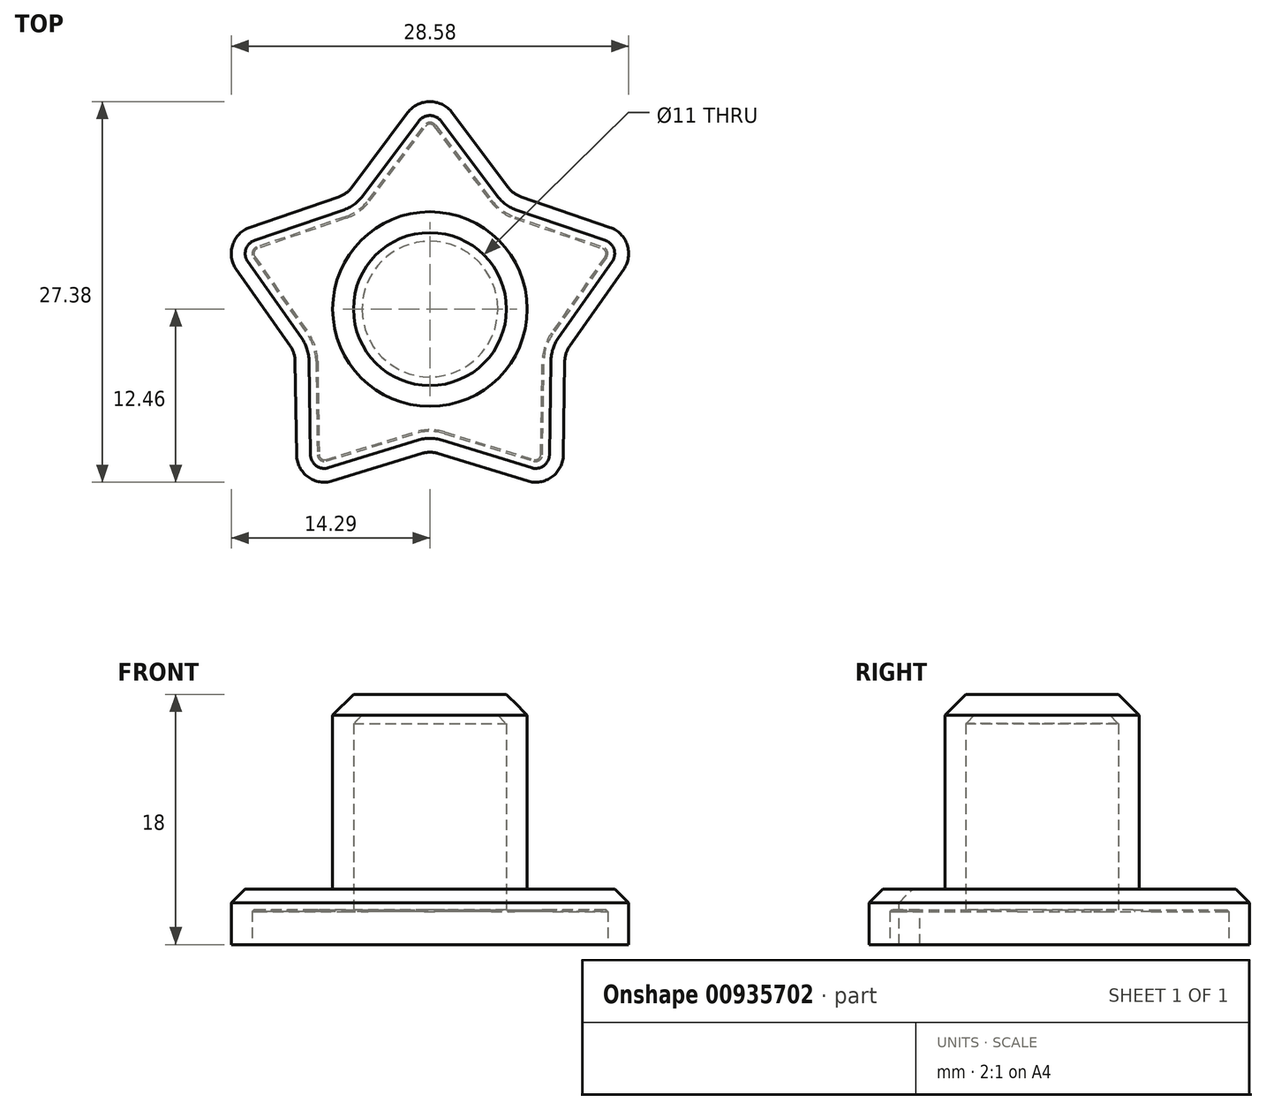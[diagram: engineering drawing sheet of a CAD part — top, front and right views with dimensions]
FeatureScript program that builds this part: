
annotation { "Feature Type Name" : "Feature", "Feature Type Description" : "" }
export const myFeature = defineFeature(function(context is Context, id is Id, definition is map)
    precondition{}
    {
        {
            var Q0;
            Q0=qCreatedBy(makeId("Top.planeOp"),FACE);
            var sketch = newSketch(context, id + "F0", { "sketchPlane" : qUnion([Q0])});
            skCircle(sketch, "E0.cCircle", {"center": v(0, 0) * mm, "radius": 8.26 * mm, "construction": true});
            skLineSegment(sketch, "E0.0", {"start": v(-6, 8.26) * mm, "end": v(6, 8.26) * mm});
            skLineSegment(sketch, "E0.1", {"start": v(6, 8.26) * mm, "end": v(9.7, -3.15) * mm});
            skLineSegment(sketch, "E0.2", {"start": v(9.7, -3.15) * mm, "end": v(0, -10.2) * mm});
            skLineSegment(sketch, "E0.3", {"start": v(0, -10.2) * mm, "end": v(-9.7, -3.15) * mm});
            skLineSegment(sketch, "E0.4", {"start": v(-9.7, -3.15) * mm, "end": v(-6, 8.26) * mm});
            skPoint(sketch, "E0.0.midPoint", {"position": v(0, 8.26) * mm});
            skCircle(sketch, "E1", {"center": v(0, 0) * mm, "radius": 7 * mm});
            skLineSegment(sketch, "E2", {"start": v(-6, 8.26) * mm, "end": v(0, 16.26) * mm});
            skLineSegment(sketch, "E3", {"start": v(0, 16.26) * mm, "end": v(6, 8.26) * mm});
            skLineSegment(sketch, "E4", {"start": v(-6, 8.26) * mm, "end": v(-15.46, 5.02) * mm});
            skLineSegment(sketch, "E5", {"start": v(-15.46, 5.02) * mm, "end": v(-9.7, -3.15) * mm});
            skLineSegment(sketch, "E6", {"start": v(-9.7, -3.15) * mm, "end": v(-9.56, -13.15) * mm});
            skLineSegment(sketch, "E7", {"start": v(-9.56, -13.15) * mm, "end": v(0, -10.2) * mm});
            skLineSegment(sketch, "E8", {"start": v(0, -10.2) * mm, "end": v(9.56, -13.15) * mm});
            skLineSegment(sketch, "E9", {"start": v(9.56, -13.15) * mm, "end": v(9.7, -3.15) * mm});
            skLineSegment(sketch, "E10", {"start": v(6, 8.26) * mm, "end": v(15.46, 5.02) * mm});
            skLineSegment(sketch, "E11", {"start": v(15.46, 5.02) * mm, "end": v(9.7, -3.15) * mm});
            skSolve(sketch);
        }
        {
            var Q0;
            Q0=makeQuery(id+"F0.imprint","IMPRINT",FACE,{"disambiguationData":[TD([[makeQuery(id+"F0.imprint","IMPRINT",EDGE,{"derivedFrom":sQuery(id+"F0.wireOp",EDGE,"E0.4")}),1.0]])]});
            var Q1;
            Q1=makeQuery(id+"F0.imprint","IMPRINT",FACE,{"disambiguationData":[TD([[makeQuery(id+"F0.imprint","IMPRINT",EDGE,{"derivedFrom":sQuery(id+"F0.wireOp",EDGE,"E0.0")}),1.0]])]});
            var Q2;
            Q2=makeQuery(id+"F0.imprint","IMPRINT",FACE,{"disambiguationData":[TD([[makeQuery(id+"F0.imprint","IMPRINT",EDGE,{"derivedFrom":sQuery(id+"F0.wireOp",EDGE,"E0.1")}),1.0]])]});
            var Q3;
            Q3=makeQuery(id+"F0.imprint","IMPRINT",FACE,{"disambiguationData":[TD([[makeQuery(id+"F0.imprint","IMPRINT",EDGE,{"derivedFrom":sQuery(id+"F0.wireOp",EDGE,"E0.0")}),-1.0]])]});
            var Q4;
            Q4=makeQuery(id+"F0.imprint","IMPRINT",FACE,{"disambiguationData":[TD([[makeQuery(id+"F0.imprint","IMPRINT",EDGE,{"derivedFrom":sQuery(id+"F0.wireOp",EDGE,"E0.2")}),1.0]])]});
            var Q5;
            Q5=makeQuery(id+"F0.imprint","IMPRINT",FACE,{"disambiguationData":[TD([[makeQuery(id+"F0.imprint","IMPRINT",EDGE,{"derivedFrom":sQuery(id+"F0.wireOp",EDGE,"E0.3")}),1.0]])]});
            var Q6;
            Q6=makeQuery(id+"F0.imprint","IMPRINT",FACE,{"disambiguationData":[TD([[makeQuery(id+"F0.imprint","IMPRINT",EDGE,{"derivedFrom":sQuery(id+"F0.wireOp",EDGE,"E1")}),1.0]])]});
            extrude(context, id + "F1", {"entities" : qUnion([Q0, Q1, Q2, Q3, Q4, Q5, Q6]), "depth" : 4 * mm, "offsetDistance" : 25 * mm});
        }
        {
            var Q0;
            Q0=makeQuery(id+"F1.opExtrude","CAP_FACE",FACE,{"disambiguationData":[OSD([sQuery(id+"F0.wireOp",EDGE,"E2"),sQuery(id+"F0.wireOp",EDGE,"E3"),sQuery(id+"F0.wireOp",EDGE,"E4"),sQuery(id+"F0.wireOp",EDGE,"E5"),sQuery(id+"F0.wireOp",EDGE,"E6"),sQuery(id+"F0.wireOp",EDGE,"E7"),sQuery(id+"F0.wireOp",EDGE,"E8"),sQuery(id+"F0.wireOp",EDGE,"E9"),sQuery(id+"F0.wireOp",EDGE,"E10"),sQuery(id+"F0.wireOp",EDGE,"E11")])],"isStart":false});
            var sketch = newSketch(context, id + "F2", { "sketchPlane" : qUnion([Q0])});
            skCircle(sketch, "E12", {"center": v(0, 0) * mm, "radius": 7 * mm});
            skSolve(sketch);
        }
        {
            var Q0;
            Q0=makeQuery(id+"F2.imprint","IMPRINT",FACE,{"disambiguationData":[TD([[makeQuery(id+"F2.imprint","IMPRINT",EDGE,{"derivedFrom":sQuery(id+"F2.wireOp",EDGE,"E12")}),1.0]])]});
            extrude(context, id + "F3", {"entities" : qUnion([Q0]), "operationType" : NewBodyOperationType.ADD, "depth" : 14 * mm, "offsetDistance" : 25 * mm});
        }
        {
            var Q0;
            Q0=makeQuery(id+"F1.opExtrude","SWEPT_EDGE",EDGE,{"disambiguationData":[OSD([sQuery(id+"F0.wireOp",EDGE,"E10"),sQuery(id+"F0.wireOp",EDGE,"E11")])]});
            var Q1;
            Q1=makeQuery(id+"F1.opExtrude","SWEPT_EDGE",EDGE,{"disambiguationData":[OSD([sQuery(id+"F0.wireOp",EDGE,"E2"),sQuery(id+"F0.wireOp",EDGE,"E3")])]});
            var Q2;
            Q2=makeQuery(id+"F1.opExtrude","SWEPT_EDGE",EDGE,{"disambiguationData":[OSD([sQuery(id+"F0.wireOp",EDGE,"E8"),sQuery(id+"F0.wireOp",EDGE,"E9")])]});
            var Q3;
            Q3=makeQuery(id+"F1.opExtrude","SWEPT_EDGE",EDGE,{"disambiguationData":[OSD([sQuery(id+"F0.wireOp",EDGE,"E6"),sQuery(id+"F0.wireOp",EDGE,"E7")])]});
            var Q4;
            Q4=makeQuery(id+"F1.opExtrude","SWEPT_EDGE",EDGE,{"disambiguationData":[OSD([sQuery(id+"F0.wireOp",EDGE,"E4"),sQuery(id+"F0.wireOp",EDGE,"E5")])]});
            var Q5;
            Q5=makeQuery(id+"F1.opExtrude","SWEPT_EDGE",EDGE,{"disambiguationData":[OSD([sQuery(id+"F0.wireOp",EDGE,"E0.3"),sQuery(id+"F0.wireOp",EDGE,"E0.4"),sQuery(id+"F0.wireOp",EDGE,"E5"),sQuery(id+"F0.wireOp",EDGE,"E6")])]});
            var Q6;
            Q6=makeQuery(id+"F1.opExtrude","SWEPT_EDGE",EDGE,{"disambiguationData":[OSD([sQuery(id+"F0.wireOp",EDGE,"E0.0"),sQuery(id+"F0.wireOp",EDGE,"E0.4"),sQuery(id+"F0.wireOp",EDGE,"E2"),sQuery(id+"F0.wireOp",EDGE,"E4")])]});
            var Q7;
            Q7=makeQuery(id+"F1.opExtrude","SWEPT_EDGE",EDGE,{"disambiguationData":[OSD([sQuery(id+"F0.wireOp",EDGE,"E0.0"),sQuery(id+"F0.wireOp",EDGE,"E0.1"),sQuery(id+"F0.wireOp",EDGE,"E3"),sQuery(id+"F0.wireOp",EDGE,"E10")])]});
            var Q8;
            Q8=makeQuery(id+"F1.opExtrude","SWEPT_EDGE",EDGE,{"disambiguationData":[OSD([sQuery(id+"F0.wireOp",EDGE,"E0.1"),sQuery(id+"F0.wireOp",EDGE,"E0.2"),sQuery(id+"F0.wireOp",EDGE,"E9"),sQuery(id+"F0.wireOp",EDGE,"E11")])]});
            var Q9;
            Q9=makeQuery(id+"F1.opExtrude","SWEPT_EDGE",EDGE,{"disambiguationData":[OSD([sQuery(id+"F0.wireOp",EDGE,"E0.2"),sQuery(id+"F0.wireOp",EDGE,"E0.3"),sQuery(id+"F0.wireOp",EDGE,"E7"),sQuery(id+"F0.wireOp",EDGE,"E8")])]});
            fillet(context, id + "F4", {"entities" : qUnion([Q0, Q1, Q2, Q3, Q4, Q5, Q6, Q7, Q8, Q9]), "radius" : 2 * mm, "tangentPropagation" : true, "allowEdgeOverflow" : false});
        }
        {
            var Q0;
            Q0=makeQuery(id+"F3.opExtrude","CAP_EDGE",EDGE,{"disambiguationData":[OSD([sQuery(id+"F2.wireOp",EDGE,"E12")])],"isStart":false});
            var Q1;
            Q1=makeQuery(id+"F3.opExtrude","CAP_EDGE",EDGE,{"disambiguationData":[OSD([sQuery(id+"F2.wireOp",EDGE,"E12")])],"isStart":true});
            chamfer(context, id + "F5", {"entities" : qUnion([Q0, Q1]), "width" : 1.5 * mm, "tangentPropagation" : true});
        }
        {
            var Q0;
            Q0=makeQuery(id+"F1.opExtrude","CAP_EDGE",EDGE,{"disambiguationData":[OSD([sQuery(id+"F0.wireOp",EDGE,"E10")])],"isStart":false});
            chamfer(context, id + "F6", {"entities" : qUnion([Q0]), "width" : 1 * mm, "tangentPropagation" : true});
        }
        {
            var Q0;
            Q0=makeQuery(id+"F1.opExtrude","CAP_FACE",FACE,{"disambiguationData":[OSD([sQuery(id+"F0.wireOp",EDGE,"E2"),sQuery(id+"F0.wireOp",EDGE,"E3"),sQuery(id+"F0.wireOp",EDGE,"E4"),sQuery(id+"F0.wireOp",EDGE,"E5"),sQuery(id+"F0.wireOp",EDGE,"E6"),sQuery(id+"F0.wireOp",EDGE,"E7"),sQuery(id+"F0.wireOp",EDGE,"E8"),sQuery(id+"F0.wireOp",EDGE,"E9"),sQuery(id+"F0.wireOp",EDGE,"E10"),sQuery(id+"F0.wireOp",EDGE,"E11")])],"isStart":true});
            shell(context, id + "F7", {"entities" : qUnion([Q0]), "thickness" : 1.5 * mm});
        }
    });
